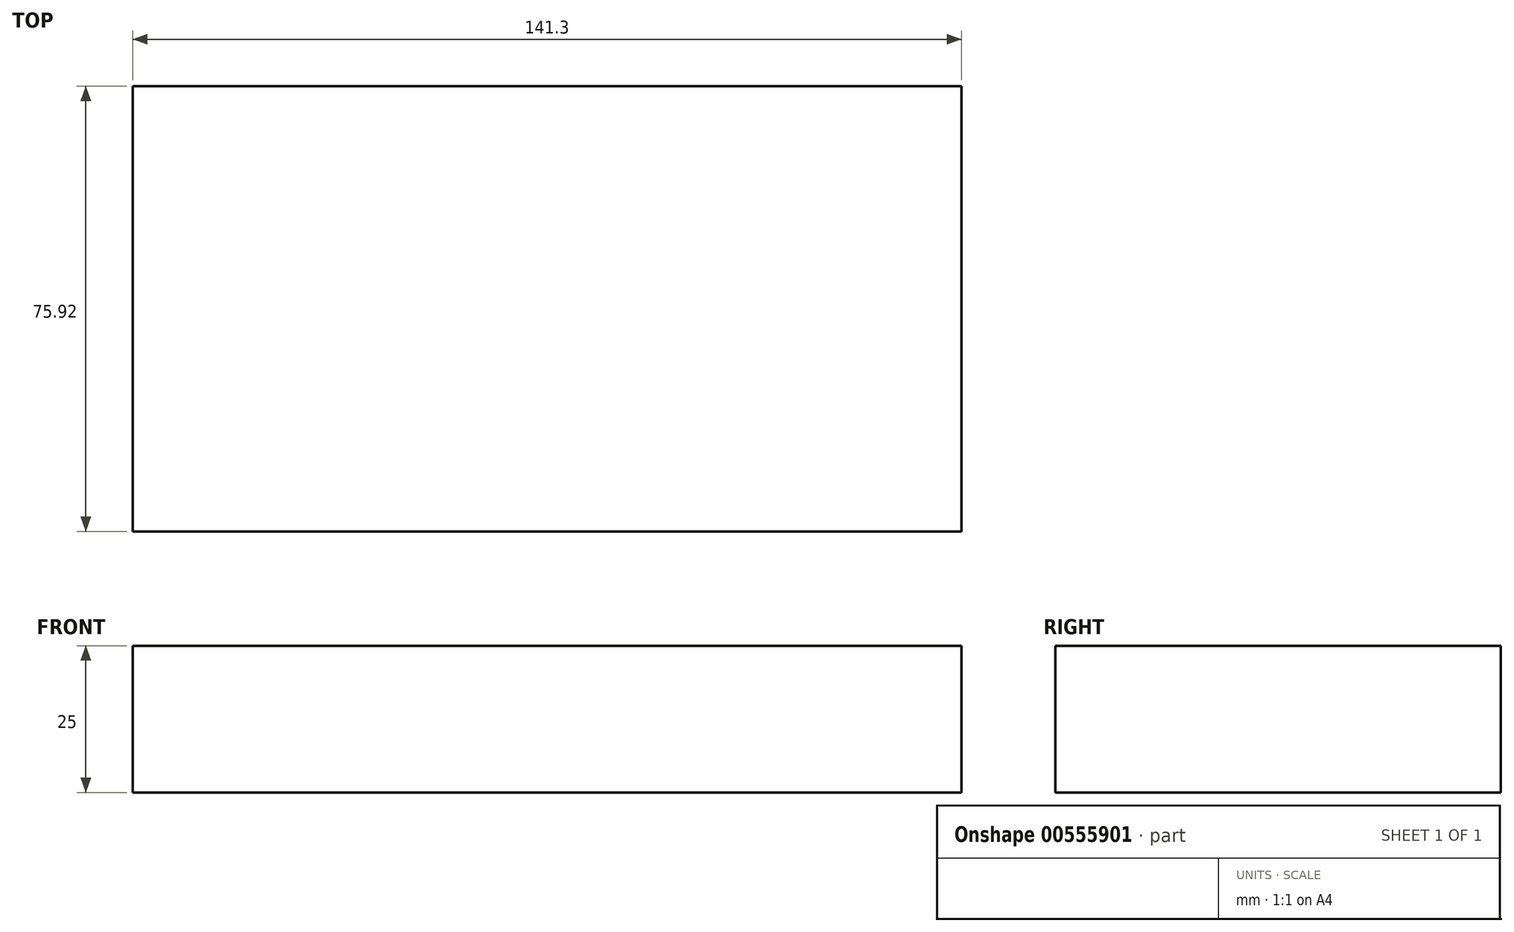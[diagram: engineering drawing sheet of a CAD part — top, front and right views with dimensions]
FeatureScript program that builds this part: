
annotation { "Feature Type Name" : "Feature", "Feature Type Description" : "" }
export const myFeature = defineFeature(function(context is Context, id is Id, definition is map)
    precondition{}
    {
        {
            var Q0;
            Q0=qCreatedBy(makeId("Top.planeOp"),FACE);
            var sketch = newSketch(context, id + "F0", { "sketchPlane" : qUnion([Q0])});
            skLineSegment(sketch, "E0.bottom", {"start": v(75.2, 0) * mm, "end": v(-66.1, 0) * mm});
            skLineSegment(sketch, "E0.top", {"start": v(75.2, 75.92) * mm, "end": v(-66.1, 75.92) * mm});
            skLineSegment(sketch, "E0.left", {"start": v(75.2, 0) * mm, "end": v(75.2, 75.92) * mm});
            skLineSegment(sketch, "E0.right", {"start": v(-66.1, 0) * mm, "end": v(-66.1, 75.92) * mm});
            skSolve(sketch);
        }
        {
            var Q0;
            Q0 = qSketchRegion(id + "F0", true);
            extrude(context, id + "F1", {"entities" : qUnion([Q0]), "depth" : 25 * mm, "offsetDistance" : 25 * mm});
        }
    });
